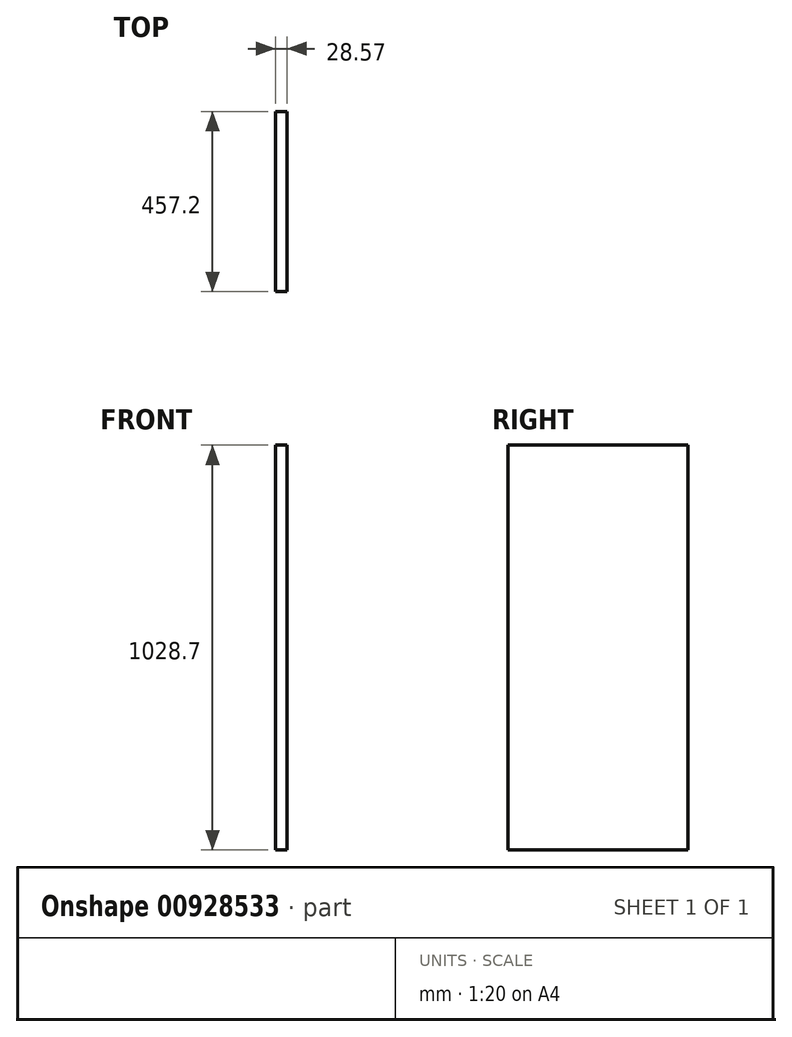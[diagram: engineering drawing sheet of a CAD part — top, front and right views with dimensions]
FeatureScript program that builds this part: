
annotation { "Feature Type Name" : "Feature", "Feature Type Description" : "" }
export const myFeature = defineFeature(function(context is Context, id is Id, definition is map)
    precondition{}
    {
        {
            var Q0;
            Q0=qCreatedBy(makeId("Right.planeOp"),FACE);
            var sketch = newSketch(context, id + "F0", { "sketchPlane" : qUnion([Q0])});
            skLineSegment(sketch, "E0.bottom", {"start": v(228.6, 514.35) * mm, "end": v(-228.6, 514.35) * mm});
            skLineSegment(sketch, "E0.top", {"start": v(228.6, -514.35) * mm, "end": v(-228.6, -514.35) * mm});
            skLineSegment(sketch, "E0.left", {"start": v(228.6, 514.35) * mm, "end": v(228.6, -514.35) * mm});
            skLineSegment(sketch, "E0.right", {"start": v(-228.6, 514.35) * mm, "end": v(-228.6, -514.35) * mm});
            skPoint(sketch, "E0.middle", {"position": v(0, 0) * mm});
            skSolve(sketch);
        }
        {
            var Q0;
            Q0=makeQuery(id+"F0.imprint","IMPRINT",FACE,{"disambiguationData":[TD([[makeQuery(id+"F0.imprint","IMPRINT",EDGE,{"derivedFrom":sQuery(id+"F0.wireOp",EDGE,"E0.bottom")}),1.0]])]});
            extrude(context, id + "F1", {"entities" : qUnion([Q0]), "depth" : 28.57 * mm, "offsetDistance" : 25.4 * mm});
        }
    });
